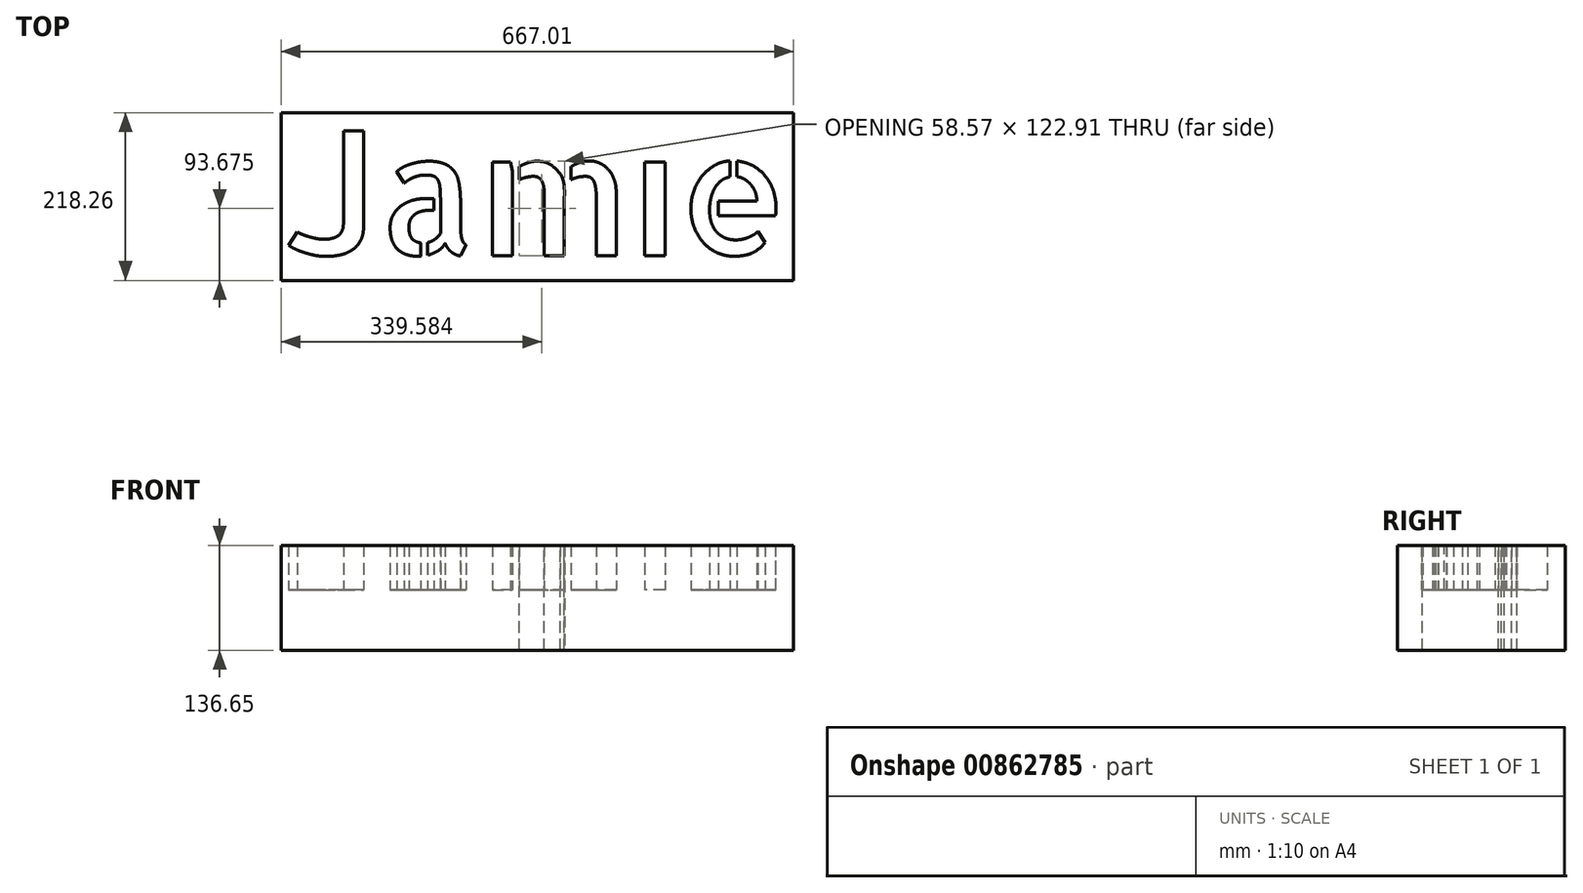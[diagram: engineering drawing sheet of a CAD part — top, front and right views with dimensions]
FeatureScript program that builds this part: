
annotation { "Feature Type Name" : "Feature", "Feature Type Description" : "" }
export const myFeature = defineFeature(function(context is Context, id is Id, definition is map)
    precondition{}
    {
        {
            var Q0;
            Q0=qCreatedBy(makeId("Top.planeOp"),FACE);
            var sketch = newSketch(context, id + "F0", { "sketchPlane" : qUnion([Q0])});
            skText(sketch, "E0", { "text": "Jamie", "fontName": "AllertaStencil-Regular.ttf"});
            skLineSegment(sketch, "E1", {"start": v(11.18, 44.95) * mm, "end": v(72.14, 29.33) * mm, "construction": true});
            skCircle(sketch, "E2", {"center": v(41.66, 37.14) * mm, "radius": 21.98 * mm, "construction": true});
            const initialGuessF0  = {"E0": [-0.14098, -0.09943, 1, 0, 0.15954]};
            skSetInitialGuess(sketch, initialGuessF0);
            skSolve(sketch);
        }
        {
            var Q0;
            Q0=makeQuery(id+"F0.imprint","IMPRINT",FACE,{"disambiguationData":[TD([[makeQuery(id+"F0.imprint","IMPRINT",EDGE,{"derivedFrom":sQuery(id+"F0.wireOp",EDGE,"E0.sketch_text.stroke-0")}),-1.0]])]});
            var Q1;
            Q1=makeQuery(id+"F0.imprint","IMPRINT",FACE,{"disambiguationData":[TD([[makeQuery(id+"F0.imprint","IMPRINT",EDGE,{"derivedFrom":sQuery(id+"F0.wireOp",EDGE,"E0.sketch_text.stroke-18")}),-1.0]])]});
            var Q2;
            Q2=makeQuery(id+"F0.imprint","IMPRINT",FACE,{"disambiguationData":[TD([[makeQuery(id+"F0.imprint","IMPRINT",EDGE,{"derivedFrom":sQuery(id+"F0.wireOp",EDGE,"E0.sketch_text.stroke-37")}),-1.0]])]});
            var Q3;
            Q3=makeQuery(id+"F0.imprint","IMPRINT",FACE,{"disambiguationData":[TD([[makeQuery(id+"F0.imprint","IMPRINT",EDGE,{"derivedFrom":sQuery(id+"F0.wireOp",EDGE,"E0.sketch_text.stroke-73")}),-1.0]])]});
            var Q4;
            Q4=makeQuery(id+"F0.imprint","IMPRINT",FACE,{"disambiguationData":[TD([[makeQuery(id+"F0.imprint","IMPRINT",EDGE,{"derivedFrom":sQuery(id+"F0.wireOp",EDGE,"E0.sketch_text.stroke-78")}),-1.0]])]});
            var Q5;
            Q5=makeQuery(id+"F0.imprint","IMPRINT",FACE,{"disambiguationData":[TD([[makeQuery(id+"F0.imprint","IMPRINT",EDGE,{"derivedFrom":sQuery(id+"F0.wireOp",EDGE,"E0.sketch_text.stroke-94")}),-1.0]])]});
            var Q6;
            Q6=makeQuery(id+"F0.imprint","IMPRINT",FACE,{"disambiguationData":[TD([[makeQuery(id+"F0.imprint","IMPRINT",EDGE,{"derivedFrom":sQuery(id+"F0.wireOp",EDGE,"E0.sketch_text.stroke-124")}),-1.0]])]});
            var Q7;
            Q7=makeQuery(id+"F0.imprint","IMPRINT",FACE,{"disambiguationData":[TD([[makeQuery(id+"F0.imprint","IMPRINT",EDGE,{"derivedFrom":sQuery(id+"F0.wireOp",EDGE,"E0.sketch_text.stroke-137")}),-1.0]])]});
            var Q8;
            Q8=makeQuery(id+"F0.imprint","IMPRINT",FACE,{"disambiguationData":[TD([[makeQuery(id+"F0.imprint","IMPRINT",EDGE,{"derivedFrom":sQuery(id+"F0.wireOp",EDGE,"E0.sketch_text.stroke-112")}),-1.0]])]});
            extrude(context, id + "F1", {"entities" : qUnion([Q0, Q1, Q2, Q3, Q4, Q5, Q6, Q7, Q8]), "depth" : 57.66 * mm, "offsetDistance" : 25.4 * mm});
        }
        {
            var Q0;
            Q0=makeQuery(id+"F1.opExtrude","CAP_FACE",FACE,{"disambiguationData":[OSD([sQuery(id+"F0.wireOp",EDGE,"E0.sketch_text.stroke-94"),sQuery(id+"F0.wireOp",EDGE,"E0.sketch_text.stroke-95"),sQuery(id+"F0.wireOp",EDGE,"E0.sketch_text.stroke-96"),sQuery(id+"F0.wireOp",EDGE,"E0.sketch_text.stroke-97"),sQuery(id+"F0.wireOp",EDGE,"E0.sketch_text.stroke-98"),sQuery(id+"F0.wireOp",EDGE,"E0.sketch_text.stroke-99"),sQuery(id+"F0.wireOp",EDGE,"E0.sketch_text.stroke-100"),sQuery(id+"F0.wireOp",EDGE,"E0.sketch_text.stroke-101"),sQuery(id+"F0.wireOp",EDGE,"E0.sketch_text.stroke-102"),sQuery(id+"F0.wireOp",EDGE,"E0.sketch_text.stroke-103"),sQuery(id+"F0.wireOp",EDGE,"E0.sketch_text.stroke-104"),sQuery(id+"F0.wireOp",EDGE,"E0.sketch_text.stroke-105"),sQuery(id+"F0.wireOp",EDGE,"E0.sketch_text.stroke-106"),sQuery(id+"F0.wireOp",EDGE,"E0.sketch_text.stroke-107"),sQuery(id+"F0.wireOp",EDGE,"E0.sketch_text.stroke-108"),sQuery(id+"F0.wireOp",EDGE,"E0.sketch_text.stroke-109"),sQuery(id+"F0.wireOp",EDGE,"E0.sketch_text.stroke-110"),sQuery(id+"F0.wireOp",EDGE,"E0.sketch_text.stroke-111")])],"isStart":false});
            var sketch = newSketch(context, id + "F2", { "sketchPlane" : qUnion([Q0])});
            skLineSegment(sketch, "E3.bottom", {"start": v(-145.32, 86.6) * mm, "end": v(521.7, 86.6) * mm});
            skLineSegment(sketch, "E3.top", {"start": v(-145.32, -131.65) * mm, "end": v(521.7, -131.65) * mm});
            skLineSegment(sketch, "E3.left", {"start": v(-145.32, 86.6) * mm, "end": v(-145.32, -131.65) * mm});
            skLineSegment(sketch, "E3.right", {"start": v(521.7, 86.6) * mm, "end": v(521.7, -131.65) * mm});
            skSolve(sketch);
        }
        {
            var Q0;
            Q0=makeQuery(id+"F2.imprint","IMPRINT",FACE,{"disambiguationData":[TD([[makeQuery(id+"F2.imprint","IMPRINT",EDGE,{"derivedFrom":sQuery(id+"F2.wireOp",EDGE,"E3.bottom")}),-1.0]])]});
            extrude(context, id + "F3", {"entities" : qUnion([Q0]), "oppositeDirection" : true, "depth" : 136.65 * mm, "offsetDistance" : 25.4 * mm});
        }
    });
